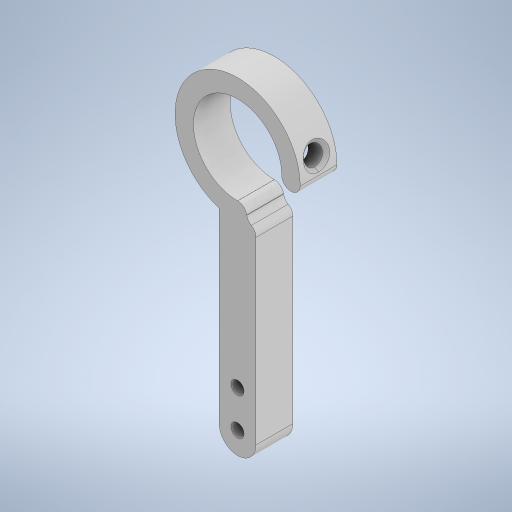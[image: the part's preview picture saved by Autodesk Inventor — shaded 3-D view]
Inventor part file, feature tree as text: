
AUTODESK INVENTOR PART (.ipt)
format: ipt  version: 2023.1 (Build 271208000, 208)  size: 326,144 bytes
history: native  units: mm
features: sketch x4, extrude x3, fillet x2, other x1, revolve x1, chamfer x1
ambient origin geometry x8: Origin, YZ Plane, XZ Plane, XY Plane, X Axis, Y Axis, Z Axis, Center Point
bodies: Body1 (feature_tree)
feature tree (12):
  other  "솔리드1"
  extrude  "돌출1"  Depth=10.0mm
  fillet  "모깎기1"  Radius=60.0mm
  revolve  "회전1"
  chamfer  "모따기1"  Distance=24.0mm
  extrude  "돌출2"  Depth=34.0mm
  fillet  "모깎기2"  Radius=10.0mm
  extrude  "돌출4"  Depth=2.5mm
  sketch  "스케치1"
  sketch  "스케치2"
  sketch  "스케치3"
  sketch  "스케치5"
